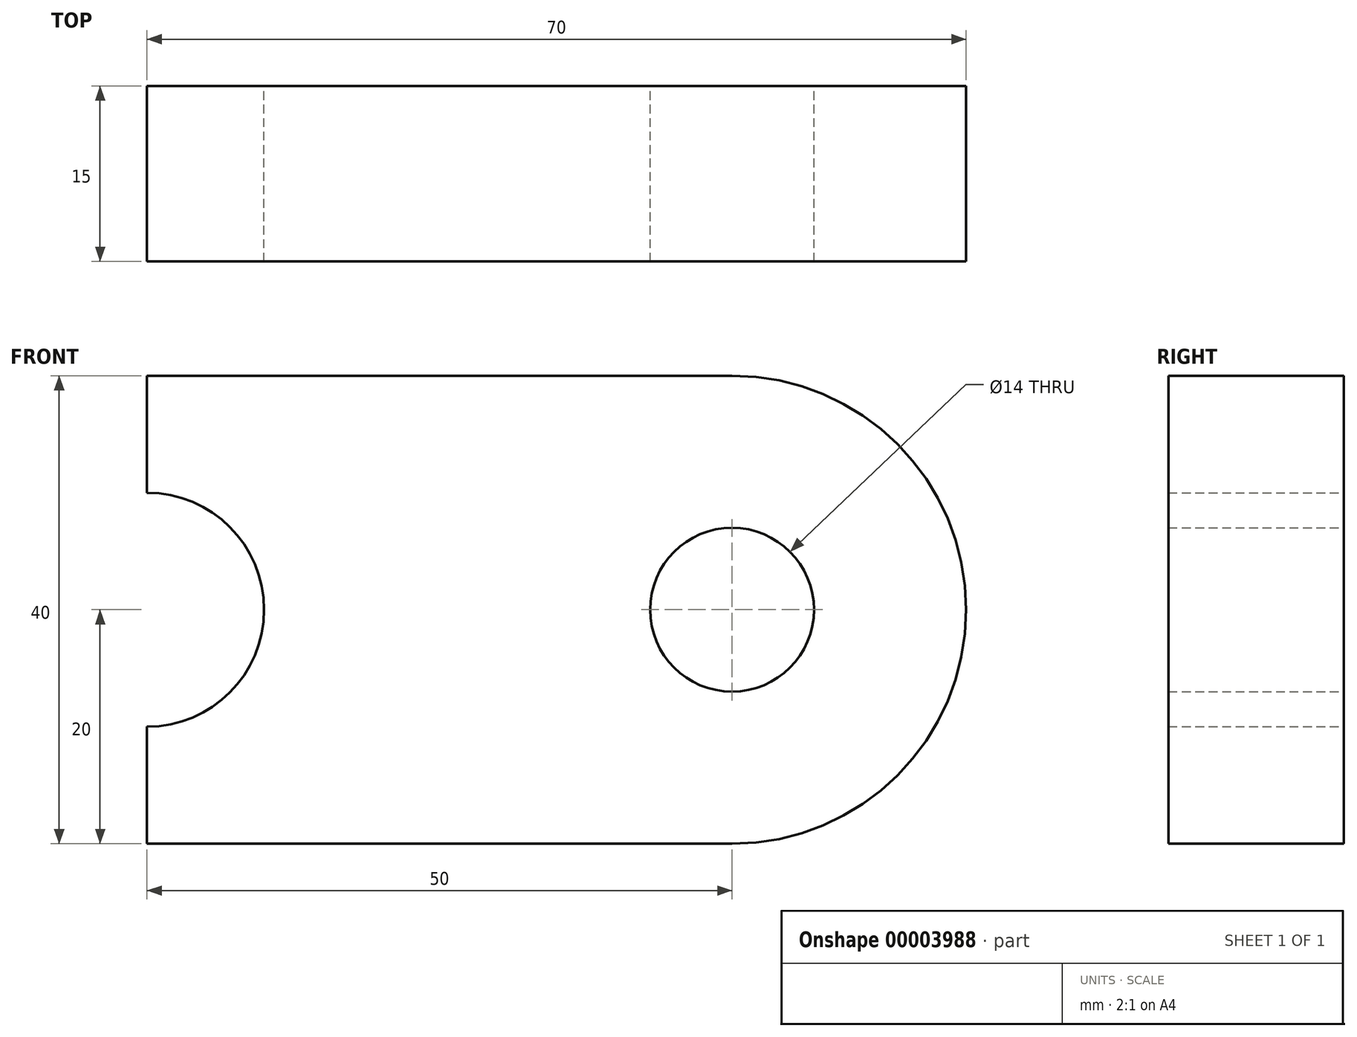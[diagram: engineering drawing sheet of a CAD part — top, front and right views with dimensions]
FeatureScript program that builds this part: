
annotation { "Feature Type Name" : "Feature", "Feature Type Description" : "" }
export const myFeature = defineFeature(function(context is Context, id is Id, definition is map)
    precondition{}
    {
        {
            var Q0;
            Q0=qCreatedBy(makeId("Front.planeOp"),FACE);
            var sketch = newSketch(context, id + "F0", { "sketchPlane" : qUnion([Q0])});
            skCircle(sketch, "E0", {"center": v(0, 0) * mm, "radius": 7 * mm});
            skCircle(sketch, "E1", {"center": v(-50, 0) * mm, "radius": 10 * mm});
            skLineSegment(sketch, "E2.bottom", {"start": v(-50, 20) * mm, "end": v(0, 20) * mm});
            skLineSegment(sketch, "E2.top", {"start": v(-50, -20) * mm, "end": v(0, -20) * mm});
            skLineSegment(sketch, "E2.left", {"start": v(-50, 20) * mm, "end": v(-50, -20) * mm});
            skLineSegment(sketch, "E2.right", {"start": v(0, 20) * mm, "end": v(0, -20) * mm});
            skArc(sketch, "E3", {"start": v(-50, -20) * mm, "mid": v(-70, 0) * mm, "end": v(-50, 20) * mm});
            skArc(sketch, "E4", {"start": v(0, -20) * mm, "mid": v(20, 0) * mm, "end": v(0, 20) * mm});
            skSolve(sketch);
        }
        {
            var Q0;
            {var subQ0=sQuery(id+"F0.wireOp",EDGE,"E3");Q0=makeQuery(id+"F0.imprint","IMPRINT",FACE,{"disambiguationData":[TD([[makeQuery(id+"F0.imprint","IMPRINT",EDGE,{"derivedFrom":subQ0}),-1.0]])]});}
            var Q1;
            {var subQ6=sQuery(id+"F0.wireOp",EDGE,"E2.bottom");Q1=makeQuery(id+"F0.imprint","IMPRINT",FACE,{"disambiguationData":[TD([[makeQuery(id+"F0.imprint","IMPRINT",EDGE,{"derivedFrom":subQ6}),-1.0]])]});}
            var Q2;
            {var subQ0=sQuery(id+"F0.wireOp",EDGE,"E4");Q2=makeQuery(id+"F0.imprint","IMPRINT",FACE,{"disambiguationData":[TD([[makeQuery(id+"F0.imprint","IMPRINT",EDGE,{"derivedFrom":subQ0}),1.0]])]});}
            extrude(context, id + "F1", {"entities" : qUnion([Q0, Q1, Q2]), "depth" : 15 * mm});
        }
    });
